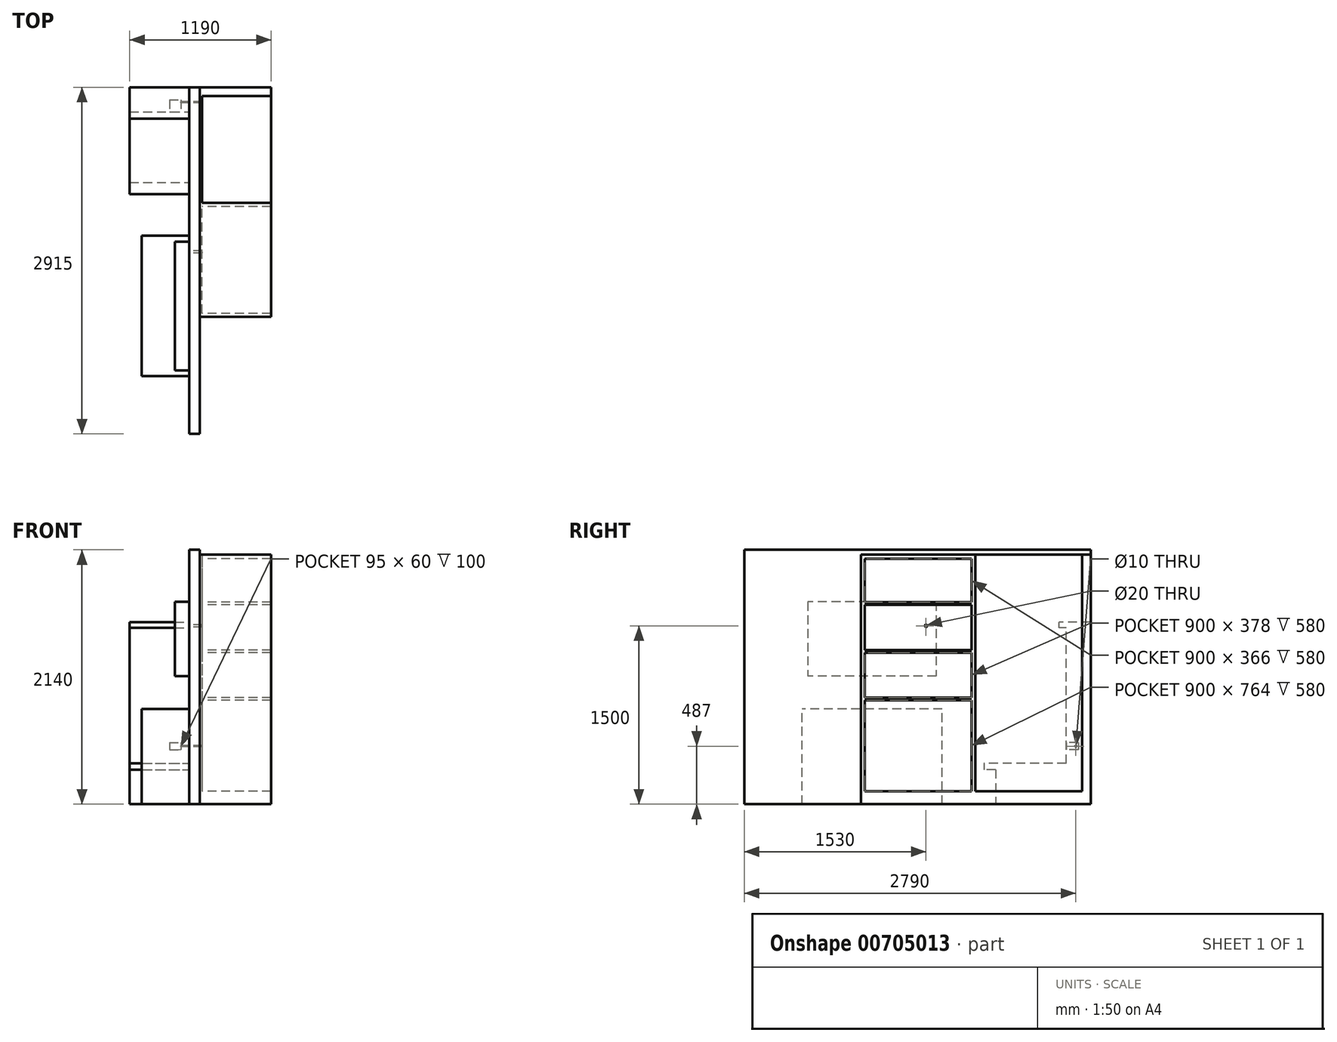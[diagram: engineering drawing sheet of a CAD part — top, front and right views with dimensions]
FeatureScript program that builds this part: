
annotation { "Feature Type Name" : "Feature", "Feature Type Description" : "" }
export const myFeature = defineFeature(function(context is Context, id is Id, definition is map)
    precondition{}
    {
        {
            var Q0;
            Q0=qCreatedBy(makeId("Right.planeOp"),FACE);
            var sketch = newSketch(context, id + "F0", { "sketchPlane" : qUnion([Q0])});
            skLineSegment(sketch, "E0.bottom", {"start": v(0, 0) * mm, "end": v(-205, 0) * mm});
            skLineSegment(sketch, "E0.top", {"start": v(0, 1140) * mm, "end": v(-205, 1140) * mm});
            skLineSegment(sketch, "E0.left", {"start": v(0, 0) * mm, "end": v(0, 1140) * mm});
            skLineSegment(sketch, "E0.right", {"start": v(-205, 0) * mm, "end": v(-205, 1140) * mm});
            skLineSegment(sketch, "E1.bottom", {"start": v(0, 1140) * mm, "end": v(-265, 1140) * mm});
            skLineSegment(sketch, "E1.top", {"start": v(0, 1187) * mm, "end": v(-265, 1187) * mm});
            skLineSegment(sketch, "E1.left", {"start": v(0, 1140) * mm, "end": v(0, 1187) * mm});
            skLineSegment(sketch, "E1.right", {"start": v(-265, 1140) * mm, "end": v(-265, 1187) * mm});
            skLineSegment(sketch, "E2.bottom", {"start": v(0, 0) * mm, "end": v(-899, 0) * mm});
            skLineSegment(sketch, "E2.top", {"start": v(0, -53) * mm, "end": v(-899, -53) * mm});
            skLineSegment(sketch, "E2.left", {"start": v(0, 0) * mm, "end": v(0, -53) * mm});
            skLineSegment(sketch, "E2.right", {"start": v(-899, 0) * mm, "end": v(-899, -53) * mm});
            skLineSegment(sketch, "E3.bottom", {"start": v(0, -53) * mm, "end": v(-799, -53) * mm});
            skLineSegment(sketch, "E3.top", {"start": v(0, -343) * mm, "end": v(-799, -343) * mm});
            skLineSegment(sketch, "E3.left", {"start": v(0, -53) * mm, "end": v(0, -343) * mm});
            skLineSegment(sketch, "E3.right", {"start": v(-799, -53) * mm, "end": v(-799, -343) * mm});
            skSolve(sketch);
        }
        {
            var Q0;
            Q0 = qSketchRegion(id + "F0", true);
            extrude(context, id + "F1", {"entities" : qUnion([Q0]), "oppositeDirection" : true, "depth" : 500 * mm, "offsetDistance" : 25 * mm});
        }
        {
            var Q0;
            Q0=makeQuery(id+"F1.opExtrude","SWEPT_FACE",FACE,{"disambiguationData":[OSD([sQuery(id+"F0.wireOp",EDGE,"E0.right")])]});
            var sketch = newSketch(context, id + "F2", { "sketchPlane" : qUnion([Q0])});
            skLineSegment(sketch, "E4.bottom", {"start": v(-165, 174) * mm, "end": v(-70, 174) * mm});
            skLineSegment(sketch, "E4.top", {"start": v(-165, 114) * mm, "end": v(-70, 114) * mm});
            skLineSegment(sketch, "E4.left", {"start": v(-165, 174) * mm, "end": v(-165, 114) * mm});
            skLineSegment(sketch, "E4.right", {"start": v(-70, 174) * mm, "end": v(-70, 114) * mm});
            skSolve(sketch);
        }
        {
            var Q0;
            Q0=makeQuery(id+"F2.imprint","IMPRINT",FACE,{"disambiguationData":[TD([[makeQuery(id+"F2.imprint","IMPRINT",EDGE,{"derivedFrom":sQuery(id+"F2.wireOp",EDGE,"E4.bottom")}),-1.0]])]});
            extrude(context, id + "F3", {"entities" : qUnion([Q0]), "operationType" : NewBodyOperationType.REMOVE, "oppositeDirection" : true, "depth" : 100 * mm, "offsetDistance" : 25 * mm});
        }
        {
            var Q0;
            Q0=qCreatedBy(makeId("Right.planeOp"),FACE);
            var sketch = newSketch(context, id + "F4", { "sketchPlane" : qUnion([Q0])});
            skLineSegment(sketch, "E5.bottom", {"start": v(0, -343) * mm, "end": v(-2915, -343) * mm});
            skLineSegment(sketch, "E5.top", {"start": v(0, 1797) * mm, "end": v(-2915, 1797) * mm});
            skLineSegment(sketch, "E5.left", {"start": v(0, -343) * mm, "end": v(0, 1797) * mm});
            skLineSegment(sketch, "E5.right", {"start": v(-2915, -343) * mm, "end": v(-2915, 1797) * mm});
            skSolve(sketch);
        }
        {
            var Q0;
            Q0=makeQuery(id+"F4.imprint","IMPRINT",FACE,{"disambiguationData":[TD([[makeQuery(id+"F4.imprint","IMPRINT",EDGE,{"derivedFrom":sQuery(id+"F4.wireOp",EDGE,"E5.bottom")}),-1.0]])]});
            extrude(context, id + "F5", {"entities" : qUnion([Q0]), "operationType" : NewBodyOperationType.ADD, "depth" : 90 * mm, "offsetDistance" : 25 * mm});
        }
        {
            var Q0;
            Q0=makeQuery(id+"F5.opExtrude","CAP_FACE",FACE,{"disambiguationData":[OSD([sQuery(id+"F4.wireOp",EDGE,"E5.bottom"),sQuery(id+"F4.wireOp",EDGE,"E5.top"),sQuery(id+"F4.wireOp",EDGE,"E5.left"),sQuery(id+"F4.wireOp",EDGE,"E5.right")])],"isStart":false});
            var sketch = newSketch(context, id + "F6", { "sketchPlane" : qUnion([Q0])});
            skLineSegment(sketch, "E6.bottom", {"start": v(0, -343) * mm, "end": v(-72, -343) * mm});
            skLineSegment(sketch, "E6.top", {"start": v(0, 1757) * mm, "end": v(-72, 1757) * mm});
            skLineSegment(sketch, "E6.left", {"start": v(0, -343) * mm, "end": v(0, 1757) * mm});
            skLineSegment(sketch, "E6.right", {"start": v(-72, -343) * mm, "end": v(-72, 1757) * mm});
            skLineSegment(sketch, "E7.bottom", {"start": v(-72, -343) * mm, "end": v(-1932, -343) * mm});
            skLineSegment(sketch, "E7.top", {"start": v(-72, -233) * mm, "end": v(-1932, -233) * mm});
            skLineSegment(sketch, "E7.left", {"start": v(-72, -343) * mm, "end": v(-72, -233) * mm});
            skLineSegment(sketch, "E7.right", {"start": v(-1932, -343) * mm, "end": v(-1932, -233) * mm});
            skLineSegment(sketch, "E8.bottom", {"start": v(-1932, -233) * mm, "end": v(-72, -233) * mm});
            skLineSegment(sketch, "E8.top", {"start": v(-1932, 1757) * mm, "end": v(-72, 1757) * mm});
            skLineSegment(sketch, "E8.left", {"start": v(-1932, -233) * mm, "end": v(-1932, 1757) * mm});
            skLineSegment(sketch, "E8.right", {"start": v(-72, -233) * mm, "end": v(-72, 1757) * mm});
            skSolve(sketch);
        }
        {
            var Q0;
            Q0=makeQuery(id+"F6.imprint","IMPRINT",FACE,{"disambiguationData":[TD([[makeQuery(id+"F6.imprint","IMPRINT",EDGE,{"derivedFrom":sQuery(id+"F6.wireOp",EDGE,"E6.bottom")}),-1.0]])]});
            var Q1;
            Q1=makeQuery(id+"F6.imprint","IMPRINT",FACE,{"disambiguationData":[TD([[makeQuery(id+"F6.imprint","IMPRINT",EDGE,{"derivedFrom":sQuery(id+"F6.wireOp",EDGE,"E7.bottom")}),-1.0]])]});
            extrude(context, id + "F7", {"entities" : qUnion([Q0, Q1]), "depth" : 600 * mm, "offsetDistance" : 25 * mm});
        }
        {
            var Q0;
            Q0 = qSketchRegion(id + "F6", true);
            extrude(context, id + "F8", {"entities" : qUnion([Q0]), "operationType" : NewBodyOperationType.ADD, "depth" : 20 * mm, "offsetDistance" : 25 * mm});
        }
        {
            var Q0;
            Q0=makeQuery(id+"F3.boolean.opBoolean","COPY",FACE,{"derivedFrom":makeQuery(id+"F3.opExtrude","SWEPT_FACE",FACE,{"disambiguationData":[OSD([sQuery(id+"F2.wireOp",EDGE,"E4.right")])]})});
            var sketch = newSketch(context, id + "F9", { "sketchPlane" : qUnion([Q0])});
            skCircle(sketch, "E9", {"center": v(125, 144) * mm, "radius": 5 * mm});
            skSolve(sketch);
        }
        {
            var Q0;
            Q0=makeQuery(id+"F9.imprint","IMPRINT",FACE,{"disambiguationData":[TD([[makeQuery(id+"F9.imprint","IMPRINT",EDGE,{"derivedFrom":sQuery(id+"F9.wireOp",EDGE,"E9")}),1.0]])]});
            var Q1;
            Q1 = qSketchRegion(id + "FzTfflDzKBxzuME_1", true);
            extrude(context, id + "F10", {"entities" : qUnion([Q0, Q1]), "operationType" : NewBodyOperationType.REMOVE, "endBound" : BoundingType.THROUGH_ALL, "oppositeDirection" : true, "depth" : 25 * mm, "offsetDistance" : 25 * mm});
        }
        {
            var Q0;
            Q0=makeQuery(id+"F8.opExtrude","CAP_FACE",FACE,{"disambiguationData":[OSD([sQuery(id+"F6.wireOp",EDGE,"E6.bottom"),sQuery(id+"F6.wireOp",EDGE,"E6.top"),sQuery(id+"F6.wireOp",EDGE,"E6.left"),sQuery(id+"F6.wireOp",EDGE,"E7.bottom"),sQuery(id+"F6.wireOp",EDGE,"E7.right"),sQuery(id+"F6.wireOp",EDGE,"E8.top"),sQuery(id+"F6.wireOp",EDGE,"E8.left")])],"isStart":false});
            var sketch = newSketch(context, id + "F11", { "sketchPlane" : qUnion([Q0])});
            skLineSegment(sketch, "E10.bottom", {"start": v(-1002, 1757) * mm, "end": v(-972, 1757) * mm});
            skLineSegment(sketch, "E10.top", {"start": v(-1002, -233) * mm, "end": v(-972, -233) * mm});
            skLineSegment(sketch, "E10.left", {"start": v(-1002, 1757) * mm, "end": v(-1002, -233) * mm});
            skLineSegment(sketch, "E10.right", {"start": v(-972, 1757) * mm, "end": v(-972, -233) * mm});
            skLineSegment(sketch, "E11.bottom", {"start": v(-1932, 1757) * mm, "end": v(-1902, 1757) * mm});
            skLineSegment(sketch, "E11.top", {"start": v(-1932, -233) * mm, "end": v(-1902, -233) * mm});
            skLineSegment(sketch, "E11.left", {"start": v(-1932, 1757) * mm, "end": v(-1932, -233) * mm});
            skLineSegment(sketch, "E11.right", {"start": v(-1902, 1757) * mm, "end": v(-1902, -233) * mm});
            skSolve(sketch);
        }
        {
            var Q0;
            Q0=makeQuery(id+"F11.imprint","IMPRINT",FACE,{"disambiguationData":[TD([[makeQuery(id+"F11.imprint","IMPRINT",EDGE,{"derivedFrom":sQuery(id+"F11.wireOp",EDGE,"E10.bottom")}),1.0]])]});
            var Q1;
            Q1=makeQuery(id+"F11.imprint","IMPRINT",FACE,{"disambiguationData":[TD([[makeQuery(id+"F11.imprint","IMPRINT",EDGE,{"derivedFrom":sQuery(id+"F11.wireOp",EDGE,"E11.bottom")}),1.0]])]});
            var Q2;
            Q2=makeQuery(id+"F7.opExtrude","CAP_FACE",FACE,{"disambiguationData":[OSD([sQuery(id+"F6.wireOp",EDGE,"E6.bottom"),sQuery(id+"F6.wireOp",EDGE,"E6.top"),sQuery(id+"F6.wireOp",EDGE,"E6.left"),sQuery(id+"F6.wireOp",EDGE,"E7.bottom"),sQuery(id+"F6.wireOp",EDGE,"E7.right"),sQuery(id+"F6.wireOp",EDGE,"E8.bottom"),sQuery(id+"F6.wireOp",EDGE,"E8.right")])],"isStart":false});
            extrude(context, id + "F12", {"entities" : qUnion([Q0, Q1]), "operationType" : NewBodyOperationType.ADD, "endBound" : BoundingType.UP_TO_SURFACE, "depth" : 25 * mm, "endBoundEntityFace" : qUnion([Q2]), "offsetDistance" : 25 * mm});
        }
        {
            var Q0;
            Q0=makeQuery(id+"F5.opExtrude","CAP_FACE",FACE,{"disambiguationData":[OSD([sQuery(id+"F4.wireOp",EDGE,"E5.bottom"),sQuery(id+"F4.wireOp",EDGE,"E5.top"),sQuery(id+"F4.wireOp",EDGE,"E5.left"),sQuery(id+"F4.wireOp",EDGE,"E5.right")])],"isStart":true});
            var sketch = newSketch(context, id + "F13", { "sketchPlane" : qUnion([Q0])});
            skLineSegment(sketch, "E12.bottom", {"start": v(1300, 1359.5) * mm, "end": v(2380, 1359.5) * mm});
            skLineSegment(sketch, "E12.top", {"start": v(1300, 734.5) * mm, "end": v(2380, 734.5) * mm});
            skLineSegment(sketch, "E12.left", {"start": v(1300, 1359.5) * mm, "end": v(1300, 734.5) * mm});
            skLineSegment(sketch, "E12.right", {"start": v(2380, 1359.5) * mm, "end": v(2380, 734.5) * mm});
            skPoint(sketch, "E12.middle", {"position": v(1840, 1047) * mm});
            skLineSegment(sketch, "E13.bottom", {"start": v(1249, -343) * mm, "end": v(2429, -343) * mm});
            skLineSegment(sketch, "E13.top", {"start": v(1249, 457) * mm, "end": v(2429, 457) * mm});
            skLineSegment(sketch, "E13.left", {"start": v(1249, -343) * mm, "end": v(1249, 457) * mm});
            skLineSegment(sketch, "E13.right", {"start": v(2429, -343) * mm, "end": v(2429, 457) * mm});
            skSolve(sketch);
        }
        {
            var Q0;
            Q0=makeQuery(id+"F13.imprint","IMPRINT",FACE,{"disambiguationData":[TD([[makeQuery(id+"F13.imprint","IMPRINT",EDGE,{"derivedFrom":sQuery(id+"F13.wireOp",EDGE,"E12.bottom")}),-1.0]])]});
            extrude(context, id + "F14", {"entities" : qUnion([Q0]), "depth" : 120 * mm, "offsetDistance" : 25 * mm});
        }
        {
            var Q0;
            Q0=makeQuery(id+"F13.imprint","IMPRINT",FACE,{"disambiguationData":[TD([[makeQuery(id+"F13.imprint","IMPRINT",EDGE,{"derivedFrom":sQuery(id+"F13.wireOp",EDGE,"E13.bottom")}),1.0]])]});
            extrude(context, id + "F15", {"entities" : qUnion([Q0]), "depth" : 400 * mm, "offsetDistance" : 25 * mm});
        }
        {
            var Q0;
            Q0=makeQuery(id+"F5.opExtrude","CAP_FACE",FACE,{"disambiguationData":[OSD([sQuery(id+"F4.wireOp",EDGE,"E5.bottom"),sQuery(id+"F4.wireOp",EDGE,"E5.top"),sQuery(id+"F4.wireOp",EDGE,"E5.left"),sQuery(id+"F4.wireOp",EDGE,"E5.right")])],"isStart":true});
            var sketch = newSketch(context, id + "F16", { "sketchPlane" : qUnion([Q0])});
            skCircle(sketch, "E14", {"center": v(1385, 1157) * mm, "radius": 10 * mm});
            skSolve(sketch);
        }
        {
            var Q0;
            Q0 = qSketchRegion(id + "F16", true);
            var Q1;
            {var subQ0=sQuery(id+"F6.wireOp",EDGE,"E8.top");var subQ1=sQuery(id+"F6.wireOp",EDGE,"E6.top");Q1=makeQuery(id+"F12.boolean.opBoolean","SPLIT",FACE,{"disambiguationData":[TD([makeQuery(id+"F12.opExtrude","SWEPT_FACE",FACE,{"disambiguationData":[OSD([sQuery(id+"F11.wireOp",EDGE,"E10.left")])]})])],"derivedFrom":makeQuery(id+"F8.opExtrude","CAP_FACE",FACE,{"disambiguationData":[OSD([sQuery(id+"F6.wireOp",EDGE,"E6.bottom"),subQ1,sQuery(id+"F6.wireOp",EDGE,"E6.left"),sQuery(id+"F6.wireOp",EDGE,"E7.bottom"),sQuery(id+"F6.wireOp",EDGE,"E7.right"),subQ0,sQuery(id+"F6.wireOp",EDGE,"E8.left")])],"isStart":false})});}
            extrude(context, id + "F17", {"entities" : qUnion([Q0]), "operationType" : NewBodyOperationType.REMOVE, "endBound" : BoundingType.UP_TO_SURFACE, "oppositeDirection" : true, "depth" : 25 * mm, "endBoundEntityFace" : qUnion([Q1]), "offsetDistance" : 25 * mm});
        }
        {
            var Q0;
            {var subQ0=sQuery(id+"F6.wireOp",EDGE,"E8.top");var subQ1=sQuery(id+"F6.wireOp",EDGE,"E6.top");Q0=makeQuery(id+"F12.boolean.opBoolean","SPLIT",FACE,{"disambiguationData":[TD([makeQuery(id+"F12.opExtrude","SWEPT_FACE",FACE,{"disambiguationData":[OSD([sQuery(id+"F11.wireOp",EDGE,"E10.left")])]})])],"derivedFrom":makeQuery(id+"F8.opExtrude","CAP_FACE",FACE,{"disambiguationData":[OSD([sQuery(id+"F6.wireOp",EDGE,"E6.bottom"),subQ1,sQuery(id+"F6.wireOp",EDGE,"E6.left"),sQuery(id+"F6.wireOp",EDGE,"E7.bottom"),sQuery(id+"F6.wireOp",EDGE,"E7.right"),subQ0,sQuery(id+"F6.wireOp",EDGE,"E8.left")])],"isStart":false})});}
            var sketch = newSketch(context, id + "F18", { "sketchPlane" : qUnion([Q0])});
            skLineSegment(sketch, "E15.bottom", {"start": v(-1902, 1757) * mm, "end": v(-1002, 1757) * mm});
            skLineSegment(sketch, "E15.top", {"start": v(-1902, 1722) * mm, "end": v(-1002, 1722) * mm});
            skLineSegment(sketch, "E15.left", {"start": v(-1902, 1757) * mm, "end": v(-1902, 1722) * mm});
            skLineSegment(sketch, "E15.right", {"start": v(-1002, 1757) * mm, "end": v(-1002, 1722) * mm});
            skLineSegment(sketch, "E16.bottom", {"start": v(-1902, 1356) * mm, "end": v(-1002, 1356) * mm});
            skLineSegment(sketch, "E16.top", {"start": v(-1902, 1334) * mm, "end": v(-1002, 1334) * mm});
            skLineSegment(sketch, "E16.left", {"start": v(-1902, 1356) * mm, "end": v(-1902, 1334) * mm});
            skLineSegment(sketch, "E16.right", {"start": v(-1002, 1356) * mm, "end": v(-1002, 1334) * mm});
            skLineSegment(sketch, "E17.bottom", {"start": v(-1902, 953) * mm, "end": v(-1002, 953) * mm});
            skLineSegment(sketch, "E17.top", {"start": v(-1902, 931) * mm, "end": v(-1002, 931) * mm});
            skLineSegment(sketch, "E17.left", {"start": v(-1902, 953) * mm, "end": v(-1902, 931) * mm});
            skLineSegment(sketch, "E17.right", {"start": v(-1002, 953) * mm, "end": v(-1002, 931) * mm});
            skLineSegment(sketch, "E18.bottom", {"start": v(-1902, 553) * mm, "end": v(-1002, 553) * mm});
            skLineSegment(sketch, "E18.top", {"start": v(-1902, 531) * mm, "end": v(-1002, 531) * mm});
            skLineSegment(sketch, "E18.left", {"start": v(-1902, 553) * mm, "end": v(-1902, 531) * mm});
            skLineSegment(sketch, "E18.right", {"start": v(-1002, 553) * mm, "end": v(-1002, 531) * mm});
            skSolve(sketch);
        }
        {
            var Q0;
            Q0 = qSketchRegion(id + "F18", true);
            var Q1;
            Q1=makeQuery(id+"F12.opExtrude","CAP_FACE",FACE,{"disambiguationData":[OSD([sQuery(id+"F11.wireOp",EDGE,"E10.bottom"),sQuery(id+"F11.wireOp",EDGE,"E10.top"),sQuery(id+"F11.wireOp",EDGE,"E10.left"),sQuery(id+"F11.wireOp",EDGE,"E10.right")])],"isStart":false});
            extrude(context, id + "F19", {"entities" : qUnion([Q0]), "operationType" : NewBodyOperationType.ADD, "endBound" : BoundingType.UP_TO_SURFACE, "depth" : 25 * mm, "endBoundEntityFace" : qUnion([Q1]), "offsetDistance" : 25 * mm});
        }
    });
